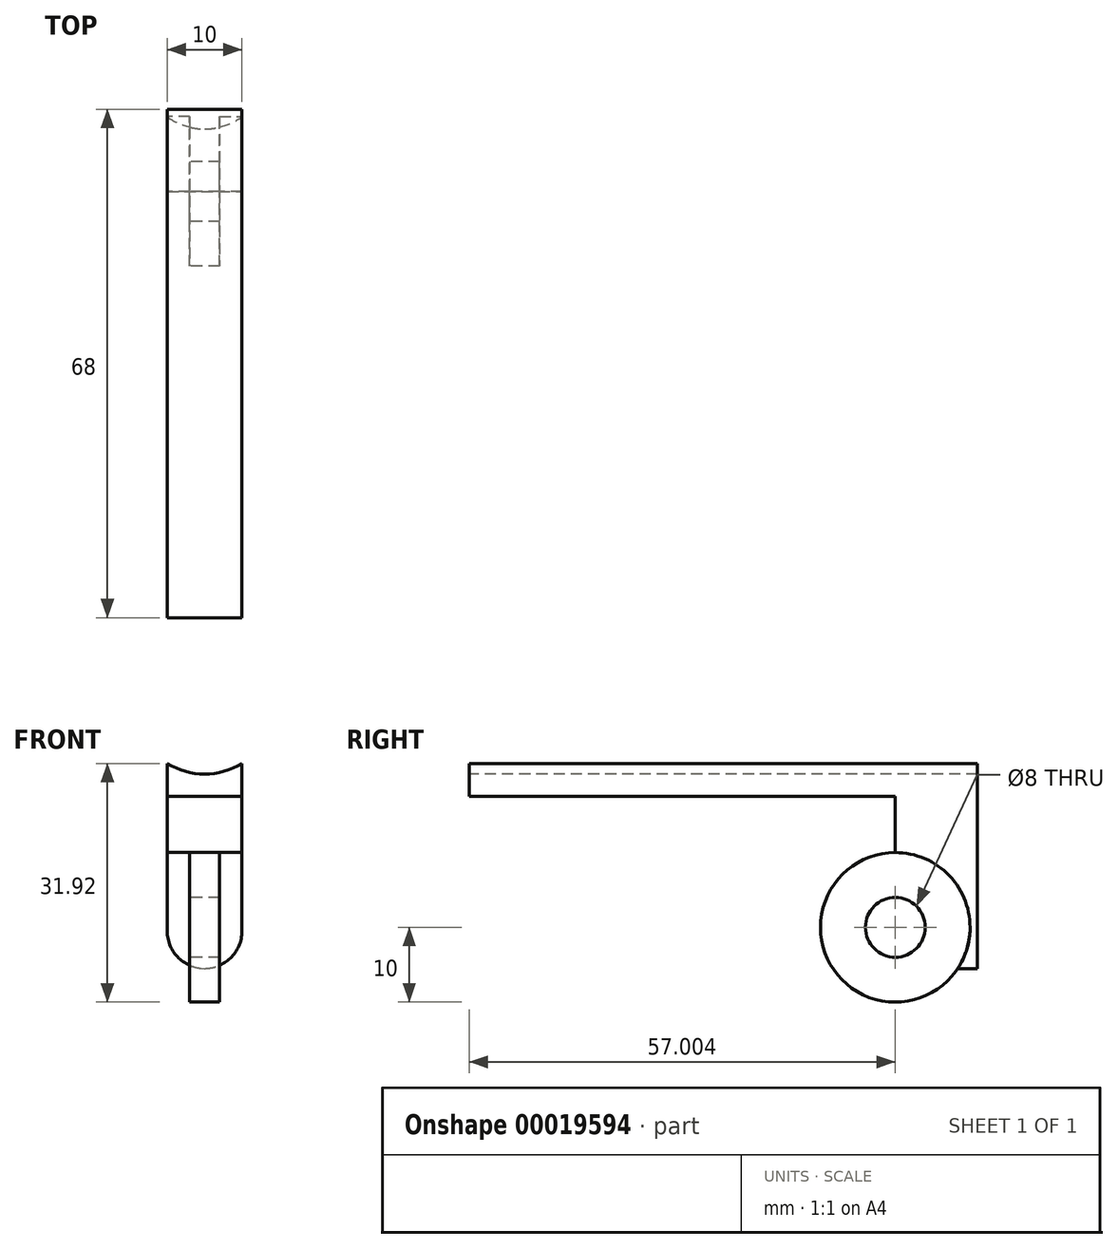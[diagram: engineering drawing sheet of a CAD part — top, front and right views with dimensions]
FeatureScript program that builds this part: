
annotation { "Feature Type Name" : "Feature", "Feature Type Description" : "" }
export const myFeature = defineFeature(function(context is Context, id is Id, definition is map)
    precondition{}
    {
        {
            var Q0;
            Q0=qCreatedBy(makeId("Top.planeOp"),FACE);
            var sketch = newSketch(context, id + "F0", { "sketchPlane" : qUnion([Q0])});
            skLineSegment(sketch, "E0.bottom", {"start": v(-5, 39.08) * mm, "end": v(5, 39.08) * mm});
            skLineSegment(sketch, "E0.top", {"start": v(-5, -28.92) * mm, "end": v(5, -28.92) * mm});
            skLineSegment(sketch, "E0.left", {"start": v(-5, 39.08) * mm, "end": v(-5, -28.92) * mm});
            skLineSegment(sketch, "E0.right", {"start": v(5, 39.08) * mm, "end": v(5, -28.92) * mm});
            skSolve(sketch);
        }
        {
            var Q0;
            Q0 = qSketchRegion(id + "F0", true);
            extrude(context, id + "F1", {"entities" : qUnion([Q0]), "depth" : 4 * mm});
        }
        {
            var Q0;
            Q0=makeQuery(id+"F1.opExtrude","CAP_FACE",FACE,{"disambiguationData":[OSD([sQuery(id+"F0.wireOp",EDGE,"E0.bottom"),sQuery(id+"F0.wireOp",EDGE,"E0.top"),sQuery(id+"F0.wireOp",EDGE,"E0.left"),sQuery(id+"F0.wireOp",EDGE,"E0.right")])],"isStart":true});
            var sketch = newSketch(context, id + "F2", { "sketchPlane" : qUnion([Q0])});
            skLineSegment(sketch, "E1.bottom", {"start": v(-5, -39.08) * mm, "end": v(5, -39.08) * mm});
            skLineSegment(sketch, "E1.top", {"start": v(-5, -28.08) * mm, "end": v(5, -28.08) * mm});
            skLineSegment(sketch, "E1.left", {"start": v(-5, -39.08) * mm, "end": v(-5, -28.08) * mm});
            skLineSegment(sketch, "E1.right", {"start": v(5, -39.08) * mm, "end": v(5, -28.08) * mm});
            skSolve(sketch);
        }
        {
            var Q0;
            Q0 = qSketchRegion(id + "F2", true);
            extrude(context, id + "F3", {"entities" : qUnion([Q0]), "operationType" : NewBodyOperationType.ADD, "depth" : 23 * mm});
        }
        {
            var Q0;
            Q0=makeQuery(id+"F3.boolean.opBoolean","MERGE",FACE,{"derivedFrom":[makeQuery(id+"F1.opExtrude","SWEPT_FACE",FACE,{"disambiguationData":[OSD([sQuery(id+"F0.wireOp",EDGE,"E0.left")])]}),makeQuery(id+"F3.opExtrude","SWEPT_FACE",FACE,{"disambiguationData":[OSD([sQuery(id+"F2.wireOp",EDGE,"E1.left")])]})]});
            var sketch = newSketch(context, id + "F4", { "sketchPlane" : qUnion([Q0])});
            skCircle(sketch, "E2", {"center": v(-28.08, -17.5) * mm, "radius": 10 * mm});
            skCircle(sketch, "E3", {"center": v(-28.08, -17.5) * mm, "radius": 4 * mm});
            skLineSegment(sketch, "E4", {"start": v(-28.08, 0) * mm, "end": v(-28.08, -17.5) * mm, "construction": true});
            skLineSegment(sketch, "E5", {"start": v(-28.08, 0) * mm, "end": v(-28.08, -7.5) * mm, "construction": true});
            skSolve(sketch);
        }
        {
            var Q0;
            {var subQ0=makeQuery(id+"F3.opExtrude","SWEPT_EDGE",EDGE,{"disambiguationData":[OSD([sQuery(id+"F0.wireOp",EDGE,"E0.left"),sQuery(id+"F2.wireOp",EDGE,"E1.top"),sQuery(id+"F2.wireOp",EDGE,"E1.left")])]});var subQ1=sQuery(id+"F4.wireOp",EDGE,"E3");var subQ3=makeQuery(id+"F4.imprint","INTERSECT",VERTEX,{"disambiguationData":[OD(0.0)],"derivedFrom":[subQ0,subQ1]});Q0=makeQuery(id+"F4.imprint","IMPRINT",FACE,{"disambiguationData":[TD([[makeQuery(id+"F4.imprint","IMPRINT",EDGE,{"disambiguationData":[TD([[subQ3,1.0]])],"derivedFrom":subQ1}),1.0]])]});}
            extrude(context, id + "F5", {"entities" : qUnion([Q0]), "operationType" : NewBodyOperationType.REMOVE, "oppositeDirection" : true, "depth" : 25.4 * mm});
        }
        {
            var Q0;
            {var subQ0=sQuery(id+"F2.wireOp",EDGE,"E1.left");var subQ1=makeQuery(id+"F3.opExtrude","CAP_EDGE",EDGE,{"disambiguationData":[OSD([subQ0])],"isStart":false});var subQ2=sQuery(id+"F4.wireOp",EDGE,"E2");var subQ3=makeQuery(id+"F4.imprint","INTERSECT",VERTEX,{"derivedFrom":[subQ1,subQ2]});Q0=makeQuery(id+"F4.imprint","IMPRINT",FACE,{"disambiguationData":[TD([[makeQuery(id+"F4.imprint","IMPRINT",EDGE,{"disambiguationData":[TD([[subQ3,-1.0]])],"derivedFrom":subQ2}),1.0]])]});}
            var Q1;
            Q1=makeQuery(id+"F3.boolean.opBoolean","MERGE",FACE,{"derivedFrom":[makeQuery(id+"F1.opExtrude","SWEPT_FACE",FACE,{"disambiguationData":[OSD([sQuery(id+"F0.wireOp",EDGE,"E0.right")])]}),makeQuery(id+"F3.opExtrude","SWEPT_FACE",FACE,{"disambiguationData":[OSD([sQuery(id+"F2.wireOp",EDGE,"E1.right")])]})]});
            extrude(context, id + "F6", {"entities" : qUnion([Q0]), "operationType" : NewBodyOperationType.ADD, "endBound" : BoundingType.UP_TO_SURFACE, "oppositeDirection" : true, "endBoundEntityFace" : qUnion([Q1]), "depth" : 25.4 * mm});
        }
        {
            var Q0;
            {var subQ0=sQuery(id+"F2.wireOp",EDGE,"E1.left");var subQ1=makeQuery(id+"F3.opExtrude","CAP_EDGE",EDGE,{"disambiguationData":[OSD([subQ0])],"isStart":false});var subQ2=sQuery(id+"F4.wireOp",EDGE,"E2");var subQ3=makeQuery(id+"F4.imprint","INTERSECT",VERTEX,{"derivedFrom":[subQ1,subQ2]});Q0=makeQuery(id+"F4.imprint","IMPRINT",FACE,{"disambiguationData":[TD([[makeQuery(id+"F4.imprint","IMPRINT",EDGE,{"disambiguationData":[TD([[subQ3,-1.0]])],"derivedFrom":subQ2}),1.0]])]});}
            var Q1;
            {var subQ0=sQuery(id+"F2.wireOp",EDGE,"E1.left");var subQ4=sQuery(id+"F4.wireOp",EDGE,"E2");var subQ6=makeQuery(id+"F3.opExtrude","CAP_EDGE",EDGE,{"disambiguationData":[OSD([subQ0])],"isStart":false});var subQ7=makeQuery(id+"F4.imprint","INTERSECT",VERTEX,{"derivedFrom":[subQ6,subQ4]});Q1=makeQuery(id+"F4.imprint","IMPRINT",FACE,{"disambiguationData":[TD([[makeQuery(id+"F4.imprint","IMPRINT",EDGE,{"disambiguationData":[TD([[subQ7,1.0]])],"derivedFrom":subQ4}),1.0]])]});}
            extrude(context, id + "F7", {"entities" : qUnion([Q0, Q1]), "operationType" : NewBodyOperationType.REMOVE, "oppositeDirection" : true, "depth" : 3 * mm});
        }
        {
            var Q0;
            Q0=makeQuery(id+"F6.boolean.opBoolean","MERGE",FACE,{"derivedFrom":[makeQuery(id+"F3.boolean.opBoolean","MERGE",FACE,{"derivedFrom":[makeQuery(id+"F1.opExtrude","SWEPT_FACE",FACE,{"disambiguationData":[OSD([sQuery(id+"F0.wireOp",EDGE,"E0.right")])]}),makeQuery(id+"F3.opExtrude","SWEPT_FACE",FACE,{"disambiguationData":[OSD([sQuery(id+"F2.wireOp",EDGE,"E1.right")])]})]}),makeQuery(id+"F6.opExtrude","CAP_FACE",FACE,{"disambiguationData":[OSD([sQuery(id+"F0.wireOp",EDGE,"E0.left"),sQuery(id+"F2.wireOp",EDGE,"E1.top"),sQuery(id+"F2.wireOp",EDGE,"E1.left"),sQuery(id+"F4.wireOp",EDGE,"E2"),sQuery(id+"F4.wireOp",EDGE,"E3")])],"isStart":false})]});
            var sketch = newSketch(context, id + "F8", { "sketchPlane" : qUnion([Q0])});
            skCircle(sketch, "E6", {"center": v(28.08, -17.5) * mm, "radius": 10 * mm});
            skCircle(sketch, "E7", {"center": v(28.08, -17.5) * mm, "radius": 4 * mm});
            skLineSegment(sketch, "E8", {"start": v(28.08, 0) * mm, "end": v(28.08, -17.5) * mm, "construction": true});
            skLineSegment(sketch, "E9", {"start": v(28.08, 0) * mm, "end": v(28.08, -7.5) * mm, "construction": true});
            skSolve(sketch);
        }
        {
            var Q0;
            {var subQ0=sQuery(id+"F8.wireOp",EDGE,"E6");Q0=makeQuery(id+"F8.imprint","IMPRINT",FACE,{"disambiguationData":[TD([[makeQuery(id+"F8.imprint","IMPRINT",EDGE,{"disambiguationData":[OD(0.0)],"derivedFrom":subQ0}),1.0]])]});}
            extrude(context, id + "F9", {"entities" : qUnion([Q0]), "operationType" : NewBodyOperationType.REMOVE, "oppositeDirection" : true, "depth" : 3 * mm});
        }
        {
            var Q0;
            Q0=makeQuery(id+"F3.opExtrude","CAP_EDGE",EDGE,{"disambiguationData":[OSD([sQuery(id+"F2.wireOp",EDGE,"E1.right")])],"isStart":false});
            var Q1;
            Q1=makeQuery(id+"F3.opExtrude","CAP_EDGE",EDGE,{"disambiguationData":[OSD([sQuery(id+"F2.wireOp",EDGE,"E1.left")])],"isStart":false});
            fillet(context, id + "F10", {"entities" : qUnion([Q0, Q1]), "radius" : 5 * mm, "tangentPropagation" : true, "allowEdgeOverflow" : false});
        }
        {
            var Q0;
            Q0=makeQuery(id+"F1.opExtrude","CAP_FACE",FACE,{"disambiguationData":[OSD([sQuery(id+"F0.wireOp",EDGE,"E0.bottom"),sQuery(id+"F0.wireOp",EDGE,"E0.top"),sQuery(id+"F0.wireOp",EDGE,"E0.left"),sQuery(id+"F0.wireOp",EDGE,"E0.right")])],"isStart":false});
            extrude(context, id + "F11", {"entities" : qUnion([Q0]), "operationType" : NewBodyOperationType.ADD, "depth" : 4 * mm});
        }
        {
            var Q0;
            {var subQ0=sQuery(id+"F0.wireOp",EDGE,"E0.top");Q0=makeQuery(id+"F11.boolean.opBoolean","MERGE",FACE,{"derivedFrom":[makeQuery(id+"F1.opExtrude","SWEPT_FACE",FACE,{"disambiguationData":[OSD([subQ0])]}),makeQuery(id+"F11.opExtrude","SWEPT_FACE",FACE,{"disambiguationData":[OSD([subQ0])]})]});}
            var sketch = newSketch(context, id + "F12", { "sketchPlane" : qUnion([Q0])});
            skCircle(sketch, "E10", {"center": v(0, 12.53) * mm, "radius": 9.53 * mm});
            skLineSegment(sketch, "E11", {"start": v(0, 12.53) * mm, "end": v(0, 3) * mm, "construction": true});
            skLineSegment(sketch, "E12", {"start": v(0, 3) * mm, "end": v(0, 0) * mm, "construction": true});
            skSolve(sketch);
        }
        {
            var Q0;
            {var subQ0=sQuery(id+"F0.wireOp",EDGE,"E0.top");var subQ5=makeQuery(id+"F11.opExtrude","CAP_EDGE",EDGE,{"disambiguationData":[OSD([subQ0])],"isStart":false});Q0=makeQuery(id+"F12.imprint","IMPRINT",FACE,{"disambiguationData":[TD([[makeQuery(id+"F12.imprint","IMPRINT",EDGE,{"derivedFrom":subQ5}),1.0]])]});}
            var Q1;
            {var subQ0=sQuery(id+"F0.wireOp",EDGE,"E0.top");var subQ5=makeQuery(id+"F11.opExtrude","CAP_EDGE",EDGE,{"disambiguationData":[OSD([subQ0])],"isStart":false});Q1=makeQuery(id+"F12.imprint","IMPRINT",FACE,{"disambiguationData":[TD([[makeQuery(id+"F12.imprint","IMPRINT",EDGE,{"derivedFrom":subQ5}),-1.0]])]});}
            extrude(context, id + "F13", {"entities" : qUnion([Q0, Q1]), "operationType" : NewBodyOperationType.REMOVE, "endBound" : BoundingType.THROUGH_ALL, "oppositeDirection" : true, "depth" : 25.4 * mm});
        }
    });
